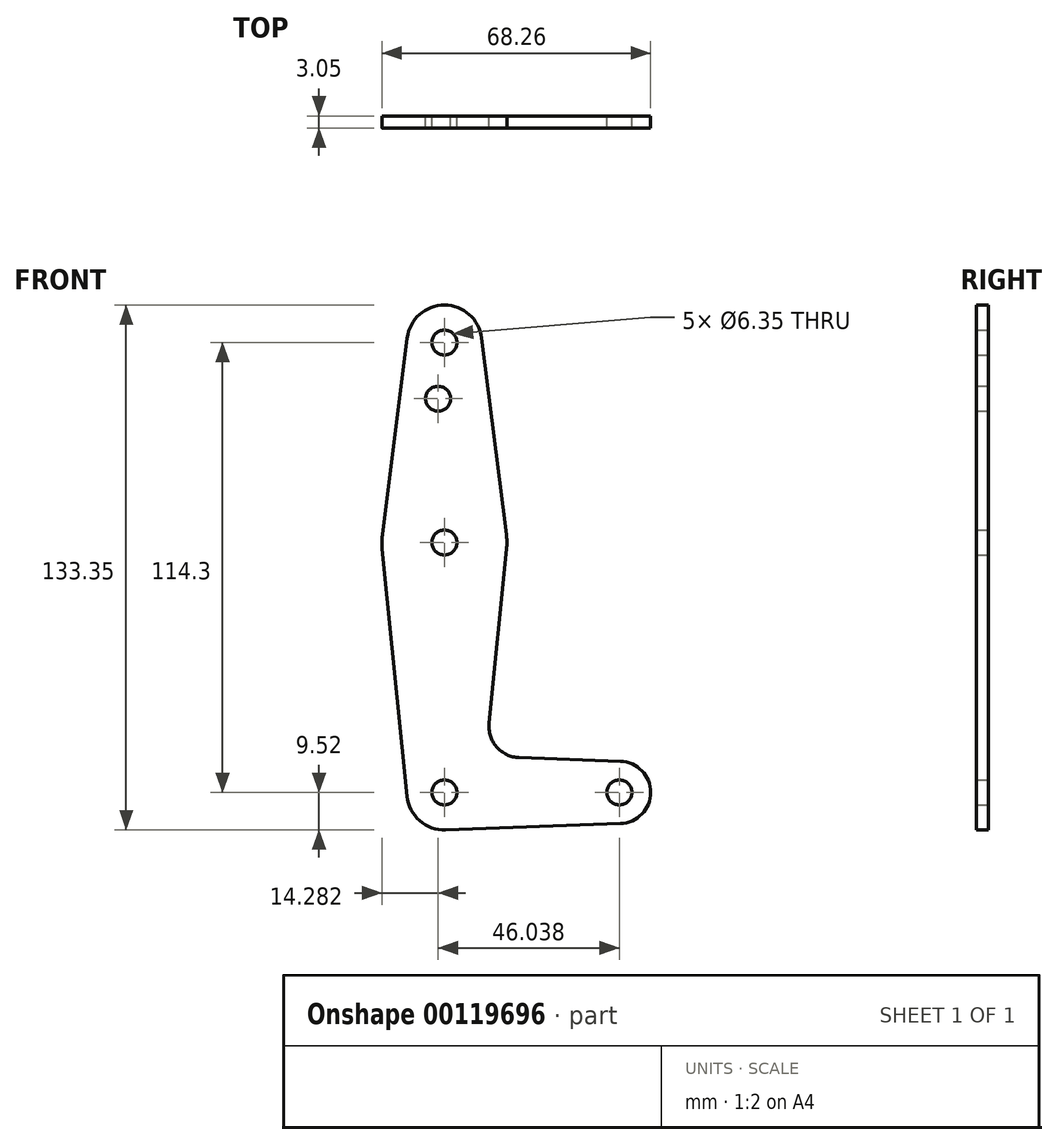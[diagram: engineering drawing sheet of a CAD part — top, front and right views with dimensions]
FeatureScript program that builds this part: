
annotation { "Feature Type Name" : "Feature", "Feature Type Description" : "" }
export const myFeature = defineFeature(function(context is Context, id is Id, definition is map)
    precondition{}
    {
        {
            var Q0;
            Q0=qCreatedBy(makeId("Front.planeOp"),FACE);
            var sketch = newSketch(context, id + "F0", { "sketchPlane" : qUnion([Q0])});
            skLineSegment(sketch, "E0", {"start": v(0, 0) * mm, "end": v(0, 63.5) * mm, "construction": true});
            skLineSegment(sketch, "E1", {"start": v(0, 63.5) * mm, "end": v(0, 114.3) * mm, "construction": true});
            skLineSegment(sketch, "E2", {"start": v(0, 0) * mm, "end": v(44.45, 0) * mm, "construction": true});
            skCircle(sketch, "E3", {"center": v(0, 114.3) * mm, "radius": 9.53 * mm});
            skCircle(sketch, "E4", {"center": v(0, 63.5) * mm, "radius": 15.88 * mm});
            skCircle(sketch, "E5", {"center": v(0, 0) * mm, "radius": 9.53 * mm});
            skCircle(sketch, "E6", {"center": v(44.45, 0) * mm, "radius": 7.94 * mm});
            skLineSegment(sketch, "E7", {"start": v(-9.45, 115.5) * mm, "end": v(-15.75, 65.48) * mm});
            skLineSegment(sketch, "E8", {"start": v(9.45, 115.5) * mm, "end": v(15.75, 65.48) * mm});
            skLineSegment(sketch, "E9", {"start": v(15.8, 61.91) * mm, "end": v(11.34, 17.6) * mm});
            skLineSegment(sketch, "E10", {"start": v(-15.8, 61.91) * mm, "end": v(-9.48, -0.95) * mm});
            skLineSegment(sketch, "E11", {"start": v(18.97, 8.85) * mm, "end": v(44.73, 7.93) * mm});
            skLineSegment(sketch, "E12", {"start": v(0.34, -9.52) * mm, "end": v(44.73, -7.93) * mm});
            skCircle(sketch, "E13", {"center": v(-1.59, 100.03) * mm, "radius": 3.18 * mm});
            skCircle(sketch, "E14", {"center": v(0, 0) * mm, "radius": 3.18 * mm});
            skCircle(sketch, "E15", {"center": v(44.45, 0) * mm, "radius": 3.18 * mm});
            skCircle(sketch, "E16", {"center": v(0, 63.5) * mm, "radius": 3.18 * mm});
            skCircle(sketch, "E17", {"center": v(0, 114.3) * mm, "radius": 3.18 * mm});
            skLineSegment(sketch, "E18.trimOffspring", {"start": v(9.57, 0) * mm, "end": v(9.48, -0.95) * mm});
            skPoint(sketch, "E19.visualSharp", {"position": v(10.5, 9.16) * mm});
            skArc(sketch, "E19.filletArc", {"start": v(11.34, 17.6) * mm, "mid": v(13.26, 11.57) * mm, "end": v(18.97, 8.85) * mm});
            skSolve(sketch);
        }
        {
            var Q0;
            Q0 = qSketchRegion(id + "F0", true);
            extrude(context, id + "F1", {"entities" : qUnion([Q0]), "depth" : 3.05 * mm});
        }
    });
